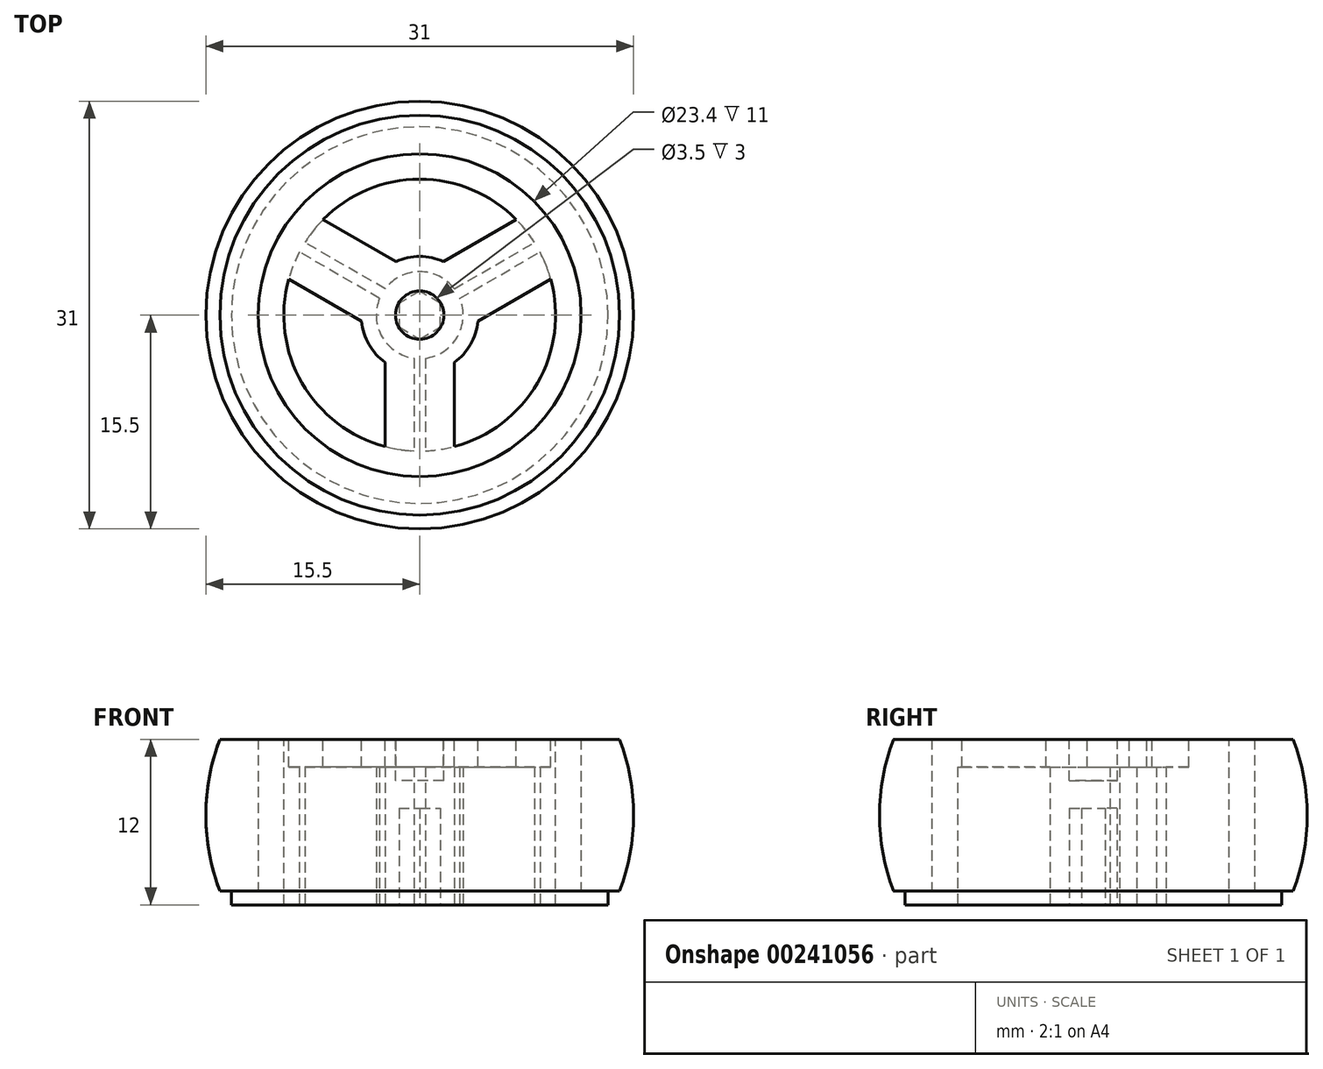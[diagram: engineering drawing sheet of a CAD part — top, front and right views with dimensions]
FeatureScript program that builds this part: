
annotation { "Feature Type Name" : "Feature", "Feature Type Description" : "" }
export const myFeature = defineFeature(function(context is Context, id is Id, definition is map)
    precondition{}
    {
        {
            var Q0;
            Q0=qCreatedBy(makeId("Top.planeOp"),FACE);
            var sketch = newSketch(context, id + "F0", { "sketchPlane" : qUnion([Q0])});
            skCircle(sketch, "E0", {"center": v(0, 0) * mm, "radius": 11.7 * mm});
            skSolve(sketch);
        }
        {
            var Q0;
            Q0=makeQuery(id+"F0.imprint","IMPRINT",FACE,{"disambiguationData":[TD([[makeQuery(id+"F0.imprint","IMPRINT",EDGE,{"derivedFrom":sQuery(id+"F0.wireOp",EDGE,"E0")}),1.0]])]});
            extrude(context, id + "F1", {"entities" : qUnion([Q0]), "depth" : 12 * mm});
        }
        {
            var Q0;
            Q0=makeQuery(id+"F1.opExtrude","CAP_FACE",FACE,{"disambiguationData":[OSD([sQuery(id+"F0.wireOp",EDGE,"E0")])],"isStart":true});
            var sketch = newSketch(context, id + "F2", { "sketchPlane" : qUnion([Q0])});
            skCircle(sketch, "E1", {"center": v(0, 0) * mm, "radius": 13.65 * mm});
            skSolve(sketch);
        }
        {
            var Q0;
            Q0=makeQuery(id+"F2.imprint","IMPRINT",FACE,{"disambiguationData":[TD([[makeQuery(id+"F2.imprint","IMPRINT",EDGE,{"derivedFrom":sQuery(id+"F2.wireOp",EDGE,"E1")}),1.0]])]});
            var Q1;
            Q1=sQuery(id+"F2.wireOp",EDGE,"E1");
            extrude(context, id + "F3", {"entities" : qUnion([Q0]), "operationType" : NewBodyOperationType.ADD, "surfaceEntities" : qUnion([Q1]), "oppositeDirection" : true, "depth" : 1 * mm});
        }
        {
            var Q0;
            Q0=makeQuery(id+"F1.opExtrude","CAP_FACE",FACE,{"disambiguationData":[OSD([sQuery(id+"F0.wireOp",EDGE,"E0")])],"isStart":false});
            var sketch = newSketch(context, id + "F4", { "sketchPlane" : qUnion([Q0])});
            skCircle(sketch, "E2", {"center": v(0, 0) * mm, "radius": 9.85 * mm});
            skSolve(sketch);
        }
        {
            var Q0;
            Q0=makeQuery(id+"F4.imprint","IMPRINT",FACE,{"disambiguationData":[TD([[makeQuery(id+"F4.imprint","IMPRINT",EDGE,{"derivedFrom":sQuery(id+"F4.wireOp",EDGE,"E2")}),1.0]])]});
            var Q1;
            {var subQ0=sQuery(id+"F0.wireOp",EDGE,"E0");Q1=makeQuery(id+"F3.boolean.opBoolean","MERGE",FACE,{"derivedFrom":[makeQuery(id+"F1.opExtrude","CAP_FACE",FACE,{"disambiguationData":[OSD([subQ0])],"isStart":true}),makeQuery(id+"F3.opExtrude","CAP_FACE",FACE,{"disambiguationData":[OSD([subQ0,sQuery(id+"F2.wireOp",EDGE,"E1")])],"isStart":true})]});}
            extrude(context, id + "F5", {"entities" : qUnion([Q0]), "operationType" : NewBodyOperationType.REMOVE, "endBound" : BoundingType.UP_TO_SURFACE, "oppositeDirection" : true, "endBoundEntityFace" : qUnion([Q1]), "depth" : 25 * mm});
        }
        {
            var Q0;
            {var subQ0=sQuery(id+"F0.wireOp",EDGE,"E0");Q0=makeQuery(id+"F3.boolean.opBoolean","MERGE",FACE,{"derivedFrom":[makeQuery(id+"F1.opExtrude","CAP_FACE",FACE,{"disambiguationData":[OSD([subQ0])],"isStart":true}),makeQuery(id+"F3.opExtrude","CAP_FACE",FACE,{"disambiguationData":[OSD([subQ0,sQuery(id+"F2.wireOp",EDGE,"E1")])],"isStart":true})]});}
            var sketch = newSketch(context, id + "F6", { "sketchPlane" : qUnion([Q0])});
            skCircle(sketch, "E3.cCircle", {"center": v(0, 0) * mm, "radius": 9.85 * mm});
            skLineSegment(sketch, "E3.0", {"start": v(0, 9.85) * mm, "end": v(8.53, -4.92) * mm, "construction": true});
            skLineSegment(sketch, "E3.1", {"start": v(8.53, -4.92) * mm, "end": v(-8.53, -4.93) * mm, "construction": true});
            skLineSegment(sketch, "E3.2", {"start": v(-8.53, -4.93) * mm, "end": v(0, 9.85) * mm, "construction": true});
            skCircle(sketch, "E4.cCircle", {"center": v(0, 0) * mm, "radius": 0.46 * mm, "construction": true});
            skLineSegment(sketch, "E4.0", {"start": v(0, 0.46) * mm, "end": v(0.4, -0.23) * mm});
            skLineSegment(sketch, "E4.1", {"start": v(0.4, -0.23) * mm, "end": v(-0.4, -0.23) * mm});
            skLineSegment(sketch, "E4.2", {"start": v(-0.4, -0.23) * mm, "end": v(0, 0.46) * mm});
            skLineSegment(sketch, "E5", {"start": v(0, 0) * mm, "end": v(8.53, -4.92) * mm, "construction": true});
            skLineSegment(sketch, "E6", {"start": v(0, 0.46) * mm, "end": v(-10.4, -5.54) * mm});
            skLineSegment(sketch, "E7", {"start": v(0.4, -0.23) * mm, "end": v(-10, -6.23) * mm});
            skLineSegment(sketch, "E8", {"start": v(-10, -6.23) * mm, "end": v(-10.4, -5.54) * mm});
            skLineSegment(sketch, "E9", {"start": v(0, 0.46) * mm, "end": v(10.4, -5.54) * mm});
            skLineSegment(sketch, "E10", {"start": v(-0.4, -0.23) * mm, "end": v(10, -6.23) * mm});
            skLineSegment(sketch, "E11", {"start": v(10, -6.23) * mm, "end": v(10.4, -5.54) * mm});
            skLineSegment(sketch, "E12", {"start": v(-0.4, -0.23) * mm, "end": v(-0.4, 11.77) * mm});
            skLineSegment(sketch, "E13", {"start": v(0.4, -0.23) * mm, "end": v(0.4, 11.77) * mm});
            skLineSegment(sketch, "E14", {"start": v(0.4, 11.77) * mm, "end": v(-0.4, 11.77) * mm});
            skSolve(sketch);
        }
        {
            var Q0;
            Q0=makeQuery(id+"F6.imprint","IMPRINT",FACE,{"disambiguationData":[TD([[makeQuery(id+"F6.imprint","IMPRINT",EDGE,{"derivedFrom":sQuery(id+"F6.wireOp",EDGE,"E4.0")}),-1.0]])]});
            var Q1;
            {var subQ5=sQuery(id+"F6.wireOp",EDGE,"E3.cCircle");var subQ7=sQuery(id+"F6.wireOp",EDGE,"E12");var subQ8=makeQuery(id+"F6.imprint","INTERSECT",VERTEX,{"derivedFrom":[subQ5,subQ7]});Q1=makeQuery(id+"F6.imprint","IMPRINT",FACE,{"disambiguationData":[TD([[makeQuery(id+"F6.imprint","IMPRINT",EDGE,{"disambiguationData":[TD([[subQ8,1.0]])],"derivedFrom":subQ5}),1.0]])]});}
            var Q2;
            {var subQ3=sQuery(id+"F6.wireOp",EDGE,"E7");var subQ5=sQuery(id+"F6.wireOp",EDGE,"E3.cCircle");var subQ6=makeQuery(id+"F6.imprint","INTERSECT",VERTEX,{"derivedFrom":[subQ5,subQ3]});Q2=makeQuery(id+"F6.imprint","IMPRINT",FACE,{"disambiguationData":[TD([[makeQuery(id+"F6.imprint","IMPRINT",EDGE,{"disambiguationData":[TD([[subQ6,1.0]])],"derivedFrom":subQ5}),1.0]])]});}
            var Q3;
            {var subQ1=sQuery(id+"F6.wireOp",EDGE,"E3.cCircle");var subQ7=sQuery(id+"F6.wireOp",EDGE,"E10");var subQ9=makeQuery(id+"F6.imprint","INTERSECT",VERTEX,{"derivedFrom":[subQ1,subQ7]});Q3=makeQuery(id+"F6.imprint","IMPRINT",FACE,{"disambiguationData":[TD([[makeQuery(id+"F6.imprint","IMPRINT",EDGE,{"disambiguationData":[TD([[subQ9,-1.0]])],"derivedFrom":subQ1}),1.0]])]});}
            var Q4;
            {var subQ0=sQuery(id+"F6.wireOp",EDGE,"E4.1");Q4=makeQuery(id+"F6.imprint","IMPRINT",FACE,{"disambiguationData":[TD([[makeQuery(id+"F6.imprint","IMPRINT",EDGE,{"derivedFrom":subQ0}),1.0]])]});}
            var Q5;
            {var subQ0=sQuery(id+"F6.wireOp",EDGE,"E4.2");Q5=makeQuery(id+"F6.imprint","IMPRINT",FACE,{"disambiguationData":[TD([[makeQuery(id+"F6.imprint","IMPRINT",EDGE,{"derivedFrom":subQ0}),1.0]])]});}
            var Q6;
            {var subQ0=sQuery(id+"F6.wireOp",EDGE,"E4.0");Q6=makeQuery(id+"F6.imprint","IMPRINT",FACE,{"disambiguationData":[TD([[makeQuery(id+"F6.imprint","IMPRINT",EDGE,{"derivedFrom":subQ0}),1.0]])]});}
            var Q7;
            Q7=makeQuery(id+"F1.opExtrude","CAP_FACE",FACE,{"disambiguationData":[OSD([sQuery(id+"F0.wireOp",EDGE,"E0")])],"isStart":false});
            extrude(context, id + "F7", {"entities" : qUnion([Q0, Q1, Q2, Q3, Q4, Q5, Q6]), "operationType" : NewBodyOperationType.ADD, "endBound" : BoundingType.UP_TO_SURFACE, "oppositeDirection" : true, "endBoundEntityFace" : qUnion([Q7]), "depth" : 25 * mm});
        }
        {
            var Q0;
            {var subQ0=sQuery(id+"F0.wireOp",EDGE,"E0");Q0=makeQuery(id+"F7.boolean.opBoolean","MERGE",FACE,{"derivedFrom":[makeQuery(id+"F1.opExtrude","CAP_FACE",FACE,{"disambiguationData":[OSD([subQ0])],"isStart":false}),makeQuery(id+"F7.opExtrude","CAP_FACE",FACE,{"disambiguationData":[OSD([subQ0])],"isStart":false})]});}
            var sketch = newSketch(context, id + "F8", { "sketchPlane" : qUnion([Q0])});
            skArc(sketch, "E15", {"start": v(-4.23, -0.45) * mm, "mid": v(-3.68, -2.12) * mm, "end": v(-2.5, -3.44) * mm});
            skLineSegment(sketch, "E16", {"start": v(-1.73, 3.88) * mm, "end": v(-8.65, 7.88) * mm});
            skLineSegment(sketch, "E17", {"start": v(-8.65, 7.88) * mm, "end": v(-11.15, 3.55) * mm});
            skLineSegment(sketch, "E18", {"start": v(-11.15, 3.55) * mm, "end": v(-4.23, -0.45) * mm});
            skPoint(sketch, "E19", {"position": v(-9.9, 5.71) * mm});
            skLineSegment(sketch, "E20", {"start": v(-9.9, 5.71) * mm, "end": v(0, 0) * mm, "construction": true});
            skLineSegment(sketch, "E21", {"start": v(-2.5, -3.44) * mm, "end": v(-2.5, -11.43) * mm});
            skLineSegment(sketch, "E22", {"start": v(-2.5, -11.43) * mm, "end": v(2.5, -11.43) * mm});
            skLineSegment(sketch, "E23", {"start": v(2.5, -11.43) * mm, "end": v(2.5, -3.44) * mm});
            skLineSegment(sketch, "E24", {"start": v(4.23, -0.45) * mm, "end": v(11.15, 3.55) * mm});
            skLineSegment(sketch, "E25", {"start": v(11.15, 3.55) * mm, "end": v(8.65, 7.88) * mm});
            skLineSegment(sketch, "E26", {"start": v(8.65, 7.88) * mm, "end": v(1.73, 3.88) * mm});
            skPoint(sketch, "E27", {"position": v(9.9, 5.71) * mm});
            skPoint(sketch, "E28", {"position": v(0, -11.43) * mm});
            skLineSegment(sketch, "E29", {"start": v(9.9, 5.71) * mm, "end": v(0, 0) * mm, "construction": true});
            skLineSegment(sketch, "E30", {"start": v(0, -11.43) * mm, "end": v(0, 0) * mm, "construction": true});
            skArc(sketch, "E31.trimOffspring", {"start": v(1.73, 3.88) * mm, "mid": v(0, 4.25) * mm, "end": v(-1.73, 3.88) * mm});
            skArc(sketch, "E32.trimOffspring", {"start": v(2.5, -3.44) * mm, "mid": v(3.68, -2.12) * mm, "end": v(4.23, -0.45) * mm});
            skSolve(sketch);
        }
        {
            var Q0;
            {var subQ9=sQuery(id+"F8.wireOp",EDGE,"E15");Q0=makeQuery(id+"F8.imprint","IMPRINT",FACE,{"disambiguationData":[TD([[makeQuery(id+"F8.imprint","IMPRINT",EDGE,{"derivedFrom":subQ9}),1.0]])]});}
            var Q1;
            {var subQ13=sQuery(id+"F8.wireOp",EDGE,"E31.trimOffspring");Q1=makeQuery(id+"F8.imprint","IMPRINT",FACE,{"disambiguationData":[TD([[makeQuery(id+"F8.imprint","IMPRINT",EDGE,{"derivedFrom":subQ13}),1.0]])]});}
            var Q2;
            {var subQ0=sQuery(id+"F8.wireOp",EDGE,"E32.trimOffspring");Q2=makeQuery(id+"F8.imprint","IMPRINT",FACE,{"disambiguationData":[TD([[makeQuery(id+"F8.imprint","IMPRINT",EDGE,{"derivedFrom":subQ0}),1.0]])]});}
            var Q3;
            {var subQ32=sQuery(id+"F8.wireOp",EDGE,"E17");Q3=makeQuery(id+"F8.imprint","IMPRINT",FACE,{"disambiguationData":[TD([[makeQuery(id+"F8.imprint","IMPRINT",EDGE,{"derivedFrom":subQ32}),1.0]])]});}
            extrude(context, id + "F9", {"entities" : qUnion([Q0, Q1, Q2, Q3]), "operationType" : NewBodyOperationType.ADD, "oppositeDirection" : true, "depth" : 2 * mm});
        }
        {
            var Q0;
            {var subQ0=sQuery(id+"F0.wireOp",EDGE,"E0");Q0=makeQuery(id+"F7.boolean.opBoolean","MERGE",FACE,{"derivedFrom":[makeQuery(id+"F3.boolean.opBoolean","MERGE",FACE,{"derivedFrom":[makeQuery(id+"F1.opExtrude","CAP_FACE",FACE,{"disambiguationData":[OSD([subQ0])],"isStart":true}),makeQuery(id+"F3.opExtrude","CAP_FACE",FACE,{"disambiguationData":[OSD([subQ0,sQuery(id+"F2.wireOp",EDGE,"E1")])],"isStart":true})]}),makeQuery(id+"F7.opExtrude","CAP_FACE",FACE,{"disambiguationData":[OSD([sQuery(id+"F6.wireOp",EDGE,"E3.cCircle"),sQuery(id+"F6.wireOp",EDGE,"E6"),sQuery(id+"F6.wireOp",EDGE,"E7"),sQuery(id+"F6.wireOp",EDGE,"E9"),sQuery(id+"F6.wireOp",EDGE,"E10"),sQuery(id+"F6.wireOp",EDGE,"E12"),sQuery(id+"F6.wireOp",EDGE,"E13")])],"isStart":true})]});}
            var sketch = newSketch(context, id + "F10", { "sketchPlane" : qUnion([Q0])});
            skCircle(sketch, "E33", {"center": v(0, 0) * mm, "radius": 3.15 * mm});
            skSolve(sketch);
        }
        {
            var Q0;
            {var subQ0=sQuery(id+"F10.wireOp",EDGE,"E33");var subQ1=makeQuery(id+"F7.opExtrude","CAP_EDGE",EDGE,{"disambiguationData":[OSD([sQuery(id+"F6.wireOp",EDGE,"E12")])],"isStart":true});var subQ2=makeQuery(id+"F10.imprint","INTERSECT",VERTEX,{"derivedFrom":[subQ1,subQ0]});Q0=makeQuery(id+"F10.imprint","IMPRINT",FACE,{"disambiguationData":[TD([[makeQuery(id+"F10.imprint","IMPRINT",EDGE,{"disambiguationData":[TD([[subQ2,-1.0]])],"derivedFrom":subQ0}),1.0]])]});}
            var Q1;
            {var subQ0=sQuery(id+"F10.wireOp",EDGE,"E33");var subQ9=makeQuery(id+"F7.opExtrude","CAP_EDGE",EDGE,{"disambiguationData":[OSD([sQuery(id+"F6.wireOp",EDGE,"E12")])],"isStart":true});var subQ11=makeQuery(id+"F10.imprint","INTERSECT",VERTEX,{"derivedFrom":[subQ9,subQ0]});Q1=makeQuery(id+"F10.imprint","IMPRINT",FACE,{"disambiguationData":[TD([[makeQuery(id+"F10.imprint","IMPRINT",EDGE,{"disambiguationData":[TD([[subQ11,1.0]])],"derivedFrom":subQ0}),1.0]])]});}
            var Q2;
            {var subQ0=sQuery(id+"F10.wireOp",EDGE,"E33");var subQ1=makeQuery(id+"F7.opExtrude","CAP_EDGE",EDGE,{"disambiguationData":[OSD([sQuery(id+"F6.wireOp",EDGE,"E7")])],"isStart":true});var subQ2=makeQuery(id+"F10.imprint","INTERSECT",VERTEX,{"derivedFrom":[subQ1,subQ0]});Q2=makeQuery(id+"F10.imprint","IMPRINT",FACE,{"disambiguationData":[TD([[makeQuery(id+"F10.imprint","IMPRINT",EDGE,{"disambiguationData":[TD([[subQ2,-1.0]])],"derivedFrom":subQ0}),1.0]])]});}
            var Q3;
            {var subQ0=sQuery(id+"F10.wireOp",EDGE,"E33");var subQ1=makeQuery(id+"F7.opExtrude","CAP_EDGE",EDGE,{"disambiguationData":[OSD([sQuery(id+"F6.wireOp",EDGE,"E13")])],"isStart":true});var subQ2=makeQuery(id+"F10.imprint","INTERSECT",VERTEX,{"derivedFrom":[subQ1,subQ0]});Q3=makeQuery(id+"F10.imprint","IMPRINT",FACE,{"disambiguationData":[TD([[makeQuery(id+"F10.imprint","IMPRINT",EDGE,{"disambiguationData":[TD([[subQ2,1.0]])],"derivedFrom":subQ0}),1.0]])]});}
            var Q4;
            {var subQ0=sQuery(id+"F8.wireOp",EDGE,"E15");var subQ1=sQuery(id+"F8.wireOp",EDGE,"E18");var subQ2=sQuery(id+"F8.wireOp",EDGE,"E21");Q4=makeQuery(id+"F9.boolean.opBoolean","SPLIT",FACE,{"disambiguationData":[TD([makeQuery(id+"F7.opExtrude","SWEPT_FACE",FACE,{"disambiguationData":[OSD([sQuery(id+"F6.wireOp",EDGE,"E6")])]})])],"derivedFrom":makeQuery(id+"F9.opExtrude","CAP_FACE",FACE,{"disambiguationData":[OSD([subQ0,sQuery(id+"F8.wireOp",EDGE,"E16"),sQuery(id+"F8.wireOp",EDGE,"E17"),subQ1,subQ2,sQuery(id+"F8.wireOp",EDGE,"E22"),sQuery(id+"F8.wireOp",EDGE,"E23"),sQuery(id+"F8.wireOp",EDGE,"E24"),sQuery(id+"F8.wireOp",EDGE,"E25"),sQuery(id+"F8.wireOp",EDGE,"E26"),sQuery(id+"F8.wireOp",EDGE,"E31.trimOffspring"),sQuery(id+"F8.wireOp",EDGE,"E32.trimOffspring")])],"isStart":false})});}
            extrude(context, id + "F11", {"entities" : qUnion([Q0, Q1, Q2, Q3]), "operationType" : NewBodyOperationType.ADD, "endBound" : BoundingType.UP_TO_SURFACE, "oppositeDirection" : true, "endBoundEntityFace" : qUnion([Q4]), "depth" : 25 * mm});
        }
        {
            var Q0;
            {var subQ0=sQuery(id+"F0.wireOp",EDGE,"E0");Q0=makeQuery(id+"F11.boolean.opBoolean","MERGE",FACE,{"derivedFrom":[makeQuery(id+"F7.boolean.opBoolean","MERGE",FACE,{"derivedFrom":[makeQuery(id+"F3.boolean.opBoolean","MERGE",FACE,{"derivedFrom":[makeQuery(id+"F1.opExtrude","CAP_FACE",FACE,{"disambiguationData":[OSD([subQ0])],"isStart":true}),makeQuery(id+"F3.opExtrude","CAP_FACE",FACE,{"disambiguationData":[OSD([subQ0,sQuery(id+"F2.wireOp",EDGE,"E1")])],"isStart":true})]}),makeQuery(id+"F7.opExtrude","CAP_FACE",FACE,{"disambiguationData":[OSD([sQuery(id+"F6.wireOp",EDGE,"E3.cCircle"),sQuery(id+"F6.wireOp",EDGE,"E6"),sQuery(id+"F6.wireOp",EDGE,"E7"),sQuery(id+"F6.wireOp",EDGE,"E9"),sQuery(id+"F6.wireOp",EDGE,"E10"),sQuery(id+"F6.wireOp",EDGE,"E12"),sQuery(id+"F6.wireOp",EDGE,"E13")])],"isStart":true})]}),makeQuery(id+"F11.opExtrude","CAP_FACE",FACE,{"disambiguationData":[OSD([sQuery(id+"F10.wireOp",EDGE,"E33")])],"isStart":true})]});}
            var sketch = newSketch(context, id + "F12", { "sketchPlane" : qUnion([Q0])});
            skCircle(sketch, "E34.cCircle", {"center": v(0, 0) * mm, "radius": 1.5 * mm, "construction": true});
            skLineSegment(sketch, "E34.0", {"start": v(1.5, 0.87) * mm, "end": v(1.5, -0.87) * mm});
            skLineSegment(sketch, "E34.1", {"start": v(1.5, -0.87) * mm, "end": v(0, -1.73) * mm});
            skLineSegment(sketch, "E34.2", {"start": v(0, -1.73) * mm, "end": v(-1.5, -0.87) * mm});
            skLineSegment(sketch, "E34.3", {"start": v(-1.5, -0.87) * mm, "end": v(-1.5, 0.87) * mm});
            skLineSegment(sketch, "E34.4", {"start": v(-1.5, 0.87) * mm, "end": v(0, 1.73) * mm});
            skLineSegment(sketch, "E34.5", {"start": v(0, 1.73) * mm, "end": v(1.5, 0.87) * mm});
            skPoint(sketch, "E34.0.midPoint", {"position": v(1.5, 0) * mm});
            skSolve(sketch);
        }
        {
            var Q0;
            Q0=makeQuery(id+"F12.imprint","IMPRINT",FACE,{"disambiguationData":[TD([[makeQuery(id+"F12.imprint","IMPRINT",EDGE,{"derivedFrom":sQuery(id+"F12.wireOp",EDGE,"E34.0")}),-1.0]])]});
            extrude(context, id + "F13", {"entities" : qUnion([Q0]), "operationType" : NewBodyOperationType.REMOVE, "oppositeDirection" : true, "depth" : 7 * mm});
        }
        {
            var Q0;
            {var subQ0=sQuery(id+"F0.wireOp",EDGE,"E0");Q0=makeQuery(id+"F9.boolean.opBoolean","MERGE",FACE,{"derivedFrom":[makeQuery(id+"F7.boolean.opBoolean","MERGE",FACE,{"derivedFrom":[makeQuery(id+"F1.opExtrude","CAP_FACE",FACE,{"disambiguationData":[OSD([subQ0])],"isStart":false}),makeQuery(id+"F7.opExtrude","CAP_FACE",FACE,{"disambiguationData":[OSD([subQ0])],"isStart":false})]}),makeQuery(id+"F9.opExtrude","CAP_FACE",FACE,{"disambiguationData":[OSD([sQuery(id+"F8.wireOp",EDGE,"E15"),sQuery(id+"F8.wireOp",EDGE,"E16"),sQuery(id+"F8.wireOp",EDGE,"E17"),sQuery(id+"F8.wireOp",EDGE,"E18"),sQuery(id+"F8.wireOp",EDGE,"E21"),sQuery(id+"F8.wireOp",EDGE,"E22"),sQuery(id+"F8.wireOp",EDGE,"E23"),sQuery(id+"F8.wireOp",EDGE,"E24"),sQuery(id+"F8.wireOp",EDGE,"E25"),sQuery(id+"F8.wireOp",EDGE,"E26"),sQuery(id+"F8.wireOp",EDGE,"E31.trimOffspring"),sQuery(id+"F8.wireOp",EDGE,"E32.trimOffspring")])],"isStart":true})]});}
            var sketch = newSketch(context, id + "F14", { "sketchPlane" : qUnion([Q0])});
            skCircle(sketch, "E35", {"center": v(0, 0) * mm, "radius": 1.75 * mm});
            skSolve(sketch);
        }
        {
            var Q0;
            Q0 = qSketchRegion(id + "F14", true);
            extrude(context, id + "F15", {"entities" : qUnion([Q0]), "operationType" : NewBodyOperationType.REMOVE, "oppositeDirection" : true, "depth" : 3 * mm});
        }
        {
            var Q0;
            Q0=qCreatedBy(makeId("Right.planeOp"),FACE);
            var sketch = newSketch(context, id + "F16", { "sketchPlane" : qUnion([Q0])});
            skLineSegment(sketch, "E36", {"start": v(-11.7, 1) * mm, "end": v(-11.7, 12) * mm});
            skLineSegment(sketch, "E37", {"start": v(11.7, 12) * mm, "end": v(11.7, 1) * mm, "construction": true});
            skLineSegment(sketch, "E38.0", {"start": v(13.65, 1) * mm, "end": v(-13.65, 1) * mm, "construction": true});
            skArc(sketch, "E39", {"start": v(-14.5, 12) * mm, "mid": v(-15.5, 6.5) * mm, "end": v(-14.5, 1) * mm});
            skPoint(sketch, "E40", {"position": v(-11.7, 6.5) * mm});
            skLineSegment(sketch, "E41", {"start": v(-14.5, 12) * mm, "end": v(-11.7, 12) * mm});
            skLineSegment(sketch, "E42", {"start": v(-14.5, 1) * mm, "end": v(-11.7, 1) * mm});
            skLineSegment(sketch, "E43", {"start": v(0, 0) * mm, "end": v(0, 18.61) * mm, "construction": true});
            skSolve(sketch);
        }
        {
            var Q0;
            Q0=makeQuery(id+"F16.imprint","IMPRINT",FACE,{"disambiguationData":[TD([[makeQuery(id+"F16.imprint","IMPRINT",EDGE,{"derivedFrom":sQuery(id+"F16.wireOp",EDGE,"E36")}),1.0]])]});
            var Q1;
            Q1=sQuery(id+"F16.wireOp",EDGE,"E43");
            revolve(context, id + "F17", {"entities" : qUnion([Q0]), "axis" : qUnion([Q1]), "revolveType" : RevolveType.FULL});
        }
    });
